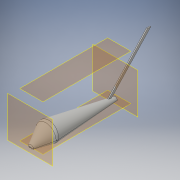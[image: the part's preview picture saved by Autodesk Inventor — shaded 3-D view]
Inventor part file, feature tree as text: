
AUTODESK INVENTOR PART (.ipt)
format: ipt  version: 2016 (Build 200138000, 138)  size: 305,152 bytes
history: native  units: in
note: dims shown in document units (in); Inventor stores cm internally (conversion verified against a paired STEP export)
features: sketch x5, plane x4, loft x3, fillet x2
ambient origin geometry x8: Origin, YZ Plane, XZ Plane, XY Plane, X Axis, Y Axis, Z Axis, Center Point
bodies: Body1 (feature_tree)
feature tree (14):
  sketch  "Sketch1"  dims[d0=5.617in d1=5.617in]
  plane  "Work Plane1"
  sketch  "Sketch2"  dims[d2=-72.0in d3=1.135in d4=1.135in d5=18.0in d6=1.135in d7=1.135in d14=0.0in d15=90.0deg]
  plane  "Work Plane2"
  loft  "Loft2"
  loft  "Loft3"
  fillet  "Fillet2"  Radius=1.135in
  fillet  "Fillet3"  [1 undecoded]
  plane  "Work Plane3"
  sketch  "Sketch4"  dims[d20=0.0in d21=90.0deg]
  plane  "Work Plane4"
  loft  "Loft5"
  sketch  "Sketch3"  dims[d16=0.0in d17=90.0deg d18=0.0in d19=90.0deg]
  sketch  "Sketch5"  dims[d23=4.0in d24=2.0in d25=1.0in d26=48.0in d31=0.0in d32=90.0deg d33=0.0in d34=90.0deg]
note: 1 required parameter value undecoded (feature->parameter linkage not recoverable at this tier; creation-order binding heuristic only, values carry confidence <= 0.55)
